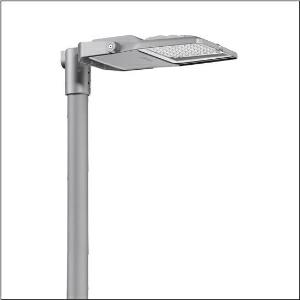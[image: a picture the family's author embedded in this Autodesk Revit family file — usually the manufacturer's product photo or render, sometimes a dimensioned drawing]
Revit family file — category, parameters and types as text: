
# Revit family: floodlight_fl_21_iq_mini___pl64_5xa7771d4e3a_aa37
name_source: partatom
category: Lighting Fixtures
units: mm (PartAtom-declared; Revit-internal decimal feet)

## family parameters
Cut with Voids When Loaded = No
Host = Face
Light Source = No
Part Type = Normal
Room Calculation Point = No
Round Connector Dimension = Use Diameter
Shared = No

## types (1)
- --- (1 x LED, 17970 lm, 143 W, 4000K)
    Apparent Load = 143 VA
    CIE Flux Codes = 28 80 98 100 100
    Color Rendering = 70
    Color Temperature = 4000K
    Default Elevation = 1800 mm
    Description = Floodlight FL 21 iQ mini, floodlight, primary light control with lens, of PMMA, primary optical cover: protective disc, of toughened safety glass, transparent, light distribution: PL64, light emission: direct distribution, installation type: surface-mounted, LED, High Power LED, rated luminous flux: 17.970lm, luminous efficacy: 126lm/W, light colour: 740, colour temperature: 4000K, control: Auto-Match, Temp-Guard, Lumen-Switch, Night-Set, Smart-Wire, Light-Fading, Desk-Remote (wireless, voltage-free reading and setting of iQ features in the workshop via application-optimized NFC function/RFID function), optimised constant luminous flux control (CLO 2.0), with terminal, 6-pole, mains connection: 220..240V, AC, 50/60Hz, start of lifetime: 143W, end of service life: 152W, reduction: 61W, luminaire housing, of diecast aluminium, powder-coated, Siteco® metallic grey (DB 702S), corrosivity category C5 mid according to DIN EN ISO 12944, sealing non-destructively replaceable, please order mast flange separately, mast bracket, of steel, galvanised, powder-coated, Siteco® metallic grey (DB 702S), protection rating (complete): IP66, insulation class (complete): insulation class II (safety insulation), certification: CE, ENEC, VDE, protection symbol: D, impact resistance: IK08, permissible operating ambient temperature: -40..+40°C, permissible operating ambient temperature for outdoor applications: -40..+50°C, standard: DIN EN 12944, LABS conformity tested according to VDMA 24364:2018-05, packaging unit: 1 piece

Light Distribution: PL64
    Height = 70 mm
    Lamp = 1 x LED
    Lamp Light Flux = 17970 lm
    Lamp Power = 143 W
    Lamp count = 1
    Length = 485 mm
    Luminous efficacy = 126 lm/W
    Manufacturer = Siteco
    ModVariant = No
    Model = 5XA7771D4E3A
    Number of Poles = 1
    OnlyDefault = Yes
    Power Factor = 1
    Product Name = Floodlight FL 21 iQ mini | PL64
    Product group = floodlight | pylon annexe
    ProductGroupID = 6200
    Protection Class = Protection class II
    Protection Degree = IP 66
    RLX_Detail_Level = 1
    RLX_Emergency_Light_Flux = 0 lm
    RLX_Emergency_Type = 0
    RLX_Emergency_Type_DB = No
    RlxData = <blob elided: 101389 chars, md5=5bab0248>
    Socket = socket
    Standby Power = 0 W
    System Light Flux = 17970 lm
    System Power = 143 W
    Type Comments = factory setting: luminous flux: 100 % | dim-lin: 254 | 730 mA
    Type Image = l_1007125.jpg
    URL = http://relux.com
    VarID = @adj_098253
    Voltage = 0 V
    Weight = 0.00 kg
    Width = 337 mm

## geometry (parser evidence)
native form markers: Blend x4, Sweep x13
no freeform markers — native parametric forms only
